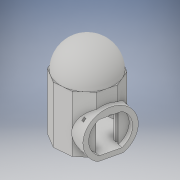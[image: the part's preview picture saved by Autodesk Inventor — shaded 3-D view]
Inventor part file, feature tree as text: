
AUTODESK INVENTOR PART (.ipt)
format: ipt  version: 2017 (Build 210142000, 142)  size: 379,392 bytes
history: native  units: in
note: dims shown in document units (in); Inventor stores cm internally (conversion verified against a paired STEP export)
features: extrude x10, sketch x8, other x4, mirror x1
ambient origin geometry x8: Origin, YZ Plane, XZ Plane, XY Plane, X Axis, Y Axis, Z Axis, Center Point
bodies: Solid1 (feature_tree), Solid2 (feature_tree)
feature tree (23):
  extrude  "bace"  Depth=1.0in TaperAngle=0.0deg
  extrude  "bace wall"  Depth=10.0in TaperAngle=0.0deg
  extrude  "bace cieiling"  Depth=2.0in
  other  "dome work plane"
  other  "dome"
  extrude  "door frame"  Depth=1.0in TaperAngle=0.0deg
  extrude  "corridor connection"  Depth=2.0in TaperAngle=0.0deg
  extrude  "hide sliding doors"  Depth=5.6918in
  extrude  "left door slot"  Depth=1.0in
  other  "door slot mirror"
  sketch  "Sketch12"  dims[d42=1.2585in d43=0.0in d44=4.0in d45=0.5833in d46=0.0625in d47=0.0625in d48=0.125in d52=0.25in d53=0.125in d54=45.0deg d55=0.0892in d56=0.0884in d57=1.0in d58=0.0in d59=1.0in d60=0.0in d61=1.0in d62=0.0in]
  extrude  "light"  Depth=1.0in TaperAngle=0.0deg
  extrude  "into wall light cut"  Depth=1.0in TaperAngle=0.0deg
  extrude  "into wall light join"  Depth=1.0in TaperAngle=0.0deg
  mirror  "Mirror1"
  other  "terminal connection parrale to door workplane"
  sketch  "Sketch1"  dims[d0=11.3835in d1=1.0in d2=0.0in]
  sketch  "Sketch2"  dims[d4=1.0in d5=10.0in d6=0.0in]
  sketch  "Sketch3"  dims[d8=1.0in d9=0.0in d16=2.0in d17=6.6667in]
  sketch  "Sketch8"  dims[d18=1.6875in d19=0.0in d20=1.0in d21=0.0in]
  sketch  "Sketch9"  dims[d22=0.25in d23=0.5in d24=6.6667in d25=2.0in d26=0.0in]
  sketch  "Sketch10"  dims[d32=4.6918in d33=5.6918in]
  sketch  "Sketch11"  dims[d34=90.0deg d38=1.0in]
